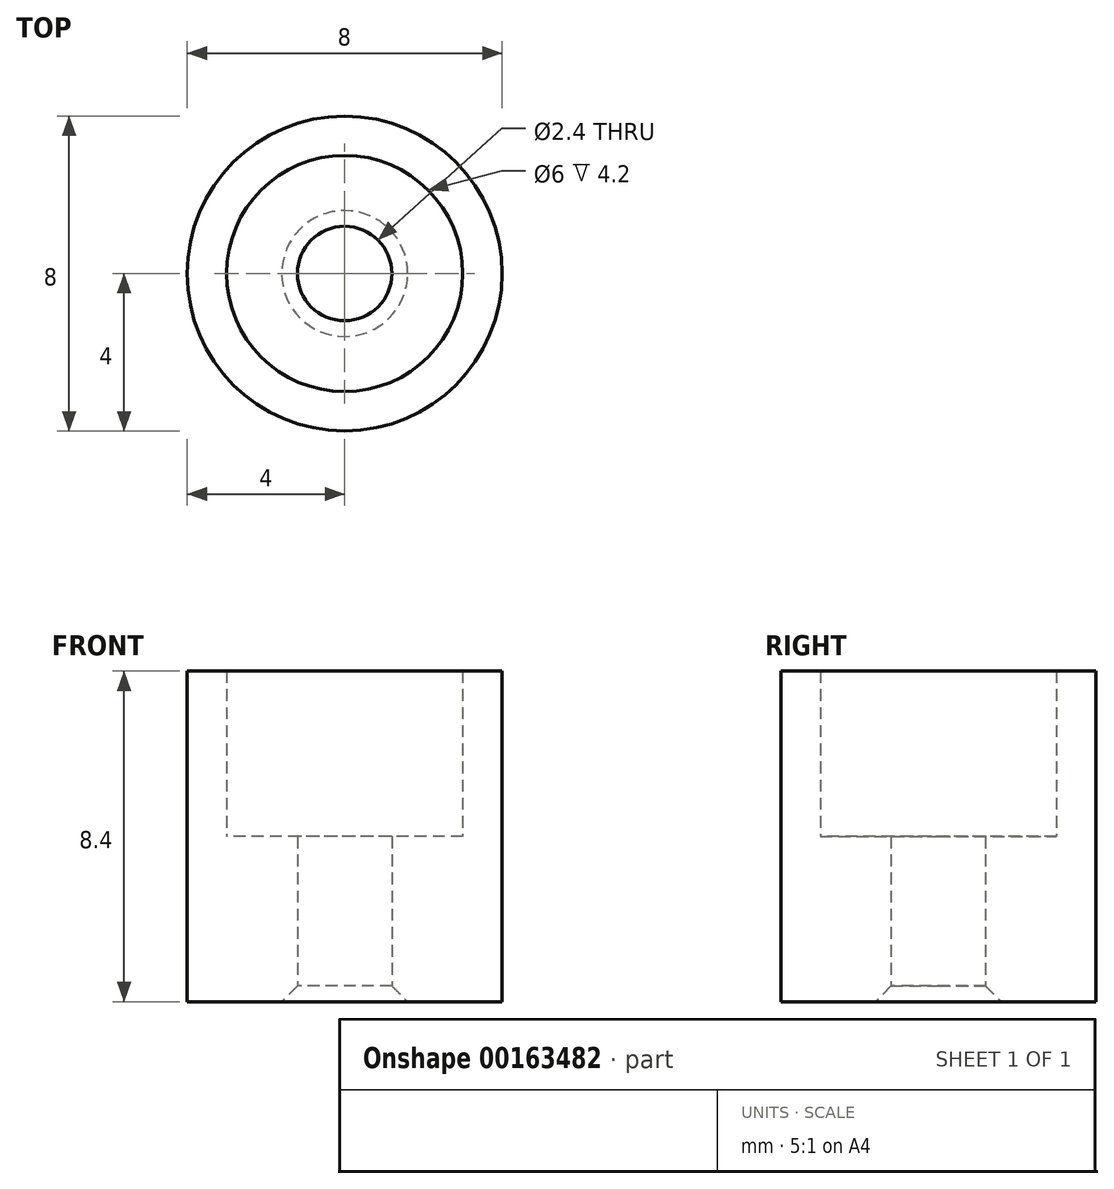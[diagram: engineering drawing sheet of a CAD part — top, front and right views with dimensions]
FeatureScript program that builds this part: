
annotation { "Feature Type Name" : "Feature", "Feature Type Description" : "" }
export const myFeature = defineFeature(function(context is Context, id is Id, definition is map)
    precondition{}
    {
        {
            var Q0;
            Q0=qCreatedBy(makeId("Top.planeOp"),FACE);
            var sketch = newSketch(context, id + "F0", { "sketchPlane" : qUnion([Q0])});
            skCircle(sketch, "E0", {"center": v(0, 0) * mm, "radius": 4 * mm});
            skCircle(sketch, "E1", {"center": v(0, 0) * mm, "radius": 1.2 * mm});
            skSolve(sketch);
        }
        {
            var Q0;
            Q0=makeQuery(id+"F0.imprint","IMPRINT",FACE,{"disambiguationData":[TD([[makeQuery(id+"F0.imprint","IMPRINT",EDGE,{"derivedFrom":sQuery(id+"F0.wireOp",EDGE,"E0")}),-1.0]])]});
            var Q1;
            Q1=makeQuery(id+"F0.imprint","IMPRINT",FACE,{"disambiguationData":[TD([[makeQuery(id+"F0.imprint","IMPRINT",EDGE,{"derivedFrom":sQuery(id+"F0.wireOp",EDGE,"E0")}),1.0]])]});
            extrude(context, id + "F1", {"entities" : qUnion([Q0, Q1]), "depth" : 8.4 * mm - 4.2 * mm});
        }
        {
            var Q0;
            Q0=makeQuery(id+"F1.opExtrude","CAP_EDGE",EDGE,{"disambiguationData":[OSD([sQuery(id+"F0.wireOp",EDGE,"E1")])],"isStart":true});
            chamfer(context, id + "F4", {"entities" : qUnion([Q0]), "width" : 0.4 * mm, "tangentPropagation" : true});
        }
        {
            var Q0;
            Q0=makeQuery(id+"F1.opExtrude","CAP_FACE",FACE,{"disambiguationData":[OSD([sQuery(id+"F0.wireOp",EDGE,"E0"),sQuery(id+"F0.wireOp",EDGE,"E1")])],"isStart":false});
            var sketch = newSketch(context, id + "F2", { "sketchPlane" : qUnion([Q0])});
            skCircle(sketch, "E2.0", {"center": v(0, 0) * mm, "radius": 4 * mm});
            skCircle(sketch, "E3", {"center": v(0, 0) * mm, "radius": 3 * mm});
            skSolve(sketch);
        }
        {
            var Q0;
            Q0=makeQuery(id+"F2.imprint","IMPRINT",FACE,{"disambiguationData":[TD([[makeQuery(id+"F2.imprint","IMPRINT",EDGE,{"derivedFrom":sQuery(id+"F2.wireOp",EDGE,"E2.0")}),1.0]])]});
            extrude(context, id + "F3", {"entities" : qUnion([Q0]), "operationType" : NewBodyOperationType.ADD, "depth" : 4.2 * mm});
        }
    });
